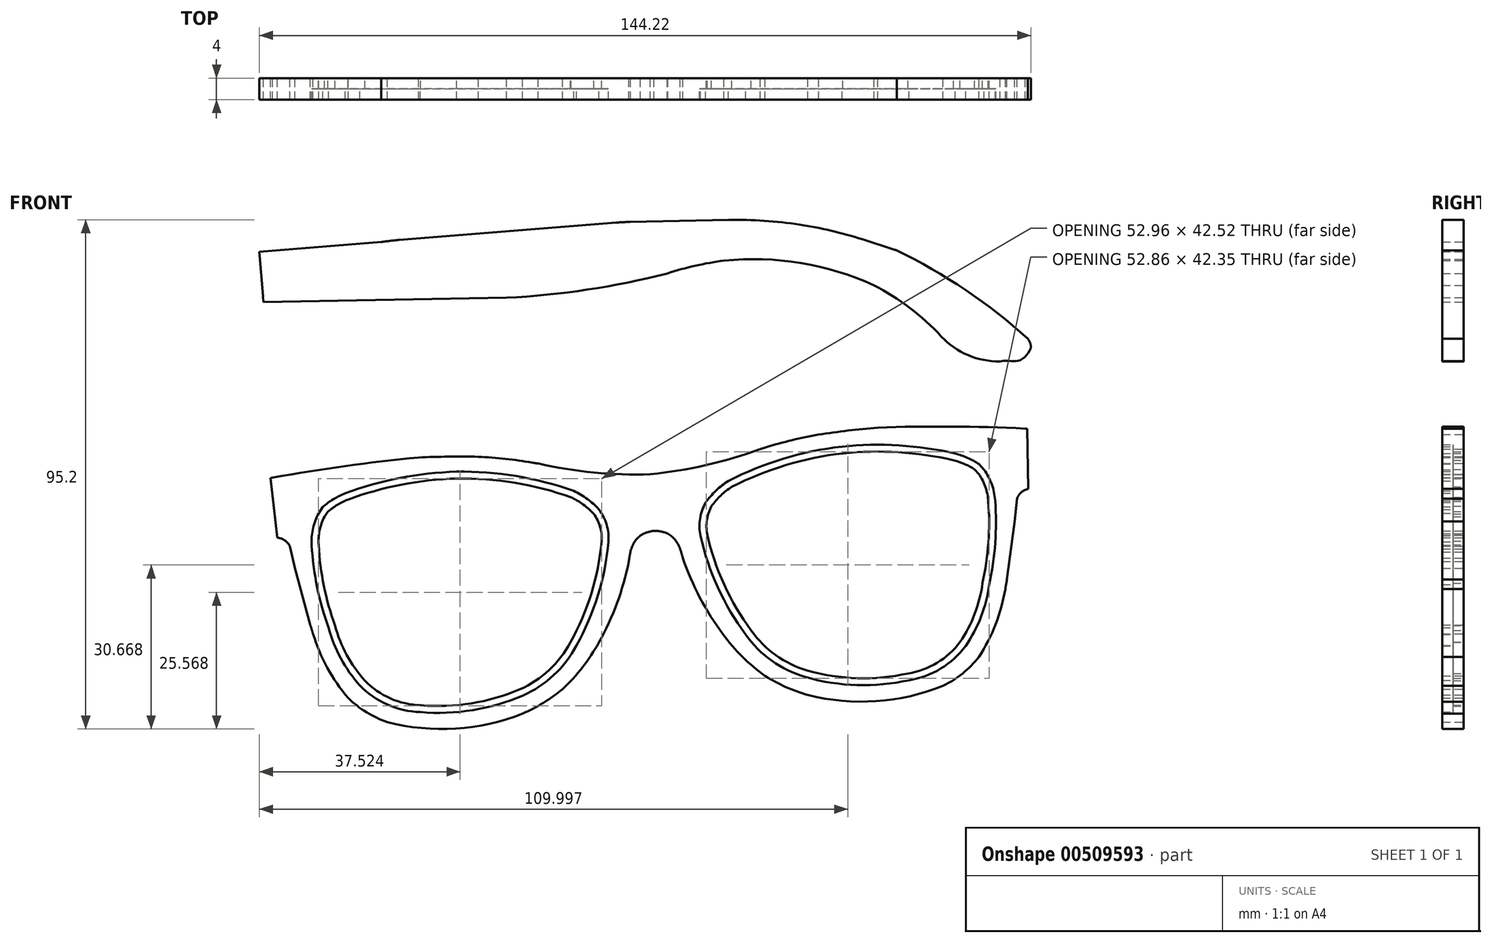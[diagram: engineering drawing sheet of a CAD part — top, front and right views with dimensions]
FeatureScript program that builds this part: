
annotation { "Feature Type Name" : "Feature", "Feature Type Description" : "" }
export const myFeature = defineFeature(function(context is Context, id is Id, definition is map)
    precondition{}
    {
        {
            var Q0;
            Q0=qCreatedBy(makeId("Front.planeOp"),FACE);
            var sketch = newSketch(context, id + "F0", { "sketchPlane" : qUnion([Q0])});
            skLineSegment(sketch, "E0", {"start": v(-3.2, 54.2) * mm, "end": v(-3.2, 54.2) * mm});
            skLineSegment(sketch, "E1", {"start": v(-1.57, 51.14) * mm, "end": v(-1.58, 51.11) * mm});
            skArc(sketch, "E2", {"start": v(-1.36, 53.99) * mm, "mid": v(-1.36, 53.99) * mm, "end": v(-1.36, 53.99) * mm});
            skArc(sketch, "E3", {"start": v(3.82, 54.3) * mm, "mid": v(3.82, 54.3) * mm, "end": v(3.82, 54.3) * mm});
            skArc(sketch, "E4", {"start": v(-1.34, 53.99) * mm, "mid": v(-1.34, 53.99) * mm, "end": v(-1.34, 53.99) * mm});
            skArc(sketch, "E5", {"start": v(-1.09, 54.17) * mm, "mid": v(-1.1, 54.16) * mm, "end": v(-1.12, 54.15) * mm});
            skArc(sketch, "E6", {"start": v(3.8, 54.29) * mm, "mid": v(3.8, 54.29) * mm, "end": v(3.8, 54.29) * mm});
            skArc(sketch, "E7", {"start": v(4.03, 54.34) * mm, "mid": v(4.03, 54.34) * mm, "end": v(4.03, 54.34) * mm});
            skArc(sketch, "E8", {"start": v(4.05, 54.34) * mm, "mid": v(4.05, 54.34) * mm, "end": v(4.05, 54.34) * mm});
            skArc(sketch, "E9", {"start": v(3.8, 54.47) * mm, "mid": v(3.78, 54.48) * mm, "end": v(3.76, 54.49) * mm});
            skLineSegment(sketch, "E10", {"start": v(-2.98, 54.16) * mm, "end": v(-2.97, 54.16) * mm});
            skLineSegment(sketch, "E11", {"start": v(-1.3, 51.11) * mm, "end": v(-1.3, 51.09) * mm});
            skArc(sketch, "E12", {"start": v(-1.1, 53.97) * mm, "mid": v(-1.1, 53.97) * mm, "end": v(-1.1, 53.97) * mm});
            skArc(sketch, "E13", {"start": v(-1.12, 53.97) * mm, "mid": v(-1.12, 53.97) * mm, "end": v(-1.12, 53.97) * mm});
            skArc(sketch, "E14", {"start": v(1.21, 56.17) * mm, "mid": v(1.21, 56.17) * mm, "end": v(1.21, 56.17) * mm});
            skLineSegment(sketch, "E15", {"start": v(-2.98, 54.16) * mm, "end": v(-2.98, 54.16) * mm});
            skLineSegment(sketch, "E16", {"start": v(-1.58, 51.14) * mm, "end": v(-1.59, 51.11) * mm});
            skLineSegment(sketch, "E17", {"start": v(-3.22, 54.2) * mm, "end": v(-3.21, 54.2) * mm});
            skArc(sketch, "E18", {"start": v(-14.4, 35.35) * mm, "mid": v(-10.5, 44.49) * mm, "end": v(-8.57, 54.23) * mm});
            skArc(sketch, "E19", {"start": v(-13.26, 34.74) * mm, "mid": v(-9.27, 44.12) * mm, "end": v(-7.3, 54.13) * mm});
            skArc(sketch, "E20", {"start": v(4.04, 54.34) * mm, "mid": v(4.04, 54.34) * mm, "end": v(4.04, 54.34) * mm});
            skArc(sketch, "E21", {"start": v(4.03, 54.34) * mm, "mid": v(4.02, 54.34) * mm, "end": v(4.02, 54.34) * mm});
            skArc(sketch, "E22", {"start": v(3.8, 54.3) * mm, "mid": v(3.8, 54.3) * mm, "end": v(3.8, 54.3) * mm});
            skArc(sketch, "E23", {"start": v(-1.35, 53.99) * mm, "mid": v(-1.35, 53.99) * mm, "end": v(-1.35, 53.99) * mm});
            skArc(sketch, "E24", {"start": v(-1.36, 54) * mm, "mid": v(-1.36, 54) * mm, "end": v(-1.37, 54) * mm});
            skArc(sketch, "E25", {"start": v(-1.3, 55.3) * mm, "mid": v(-2.53, 53.92) * mm, "end": v(-3.19, 52.2) * mm});
            skArc(sketch, "E26", {"start": v(-1.13, 53.97) * mm, "mid": v(-1.13, 53.97) * mm, "end": v(-1.13, 53.97) * mm});
            skArc(sketch, "E27", {"start": v(-1.11, 53.97) * mm, "mid": v(-1.11, 53.97) * mm, "end": v(-1.11, 53.97) * mm});
            skArc(sketch, "E28", {"start": v(-35.67, 65.95) * mm, "mid": v(-46.01, 64.8) * mm, "end": v(-56.04, 62) * mm});
            skArc(sketch, "E29", {"start": v(-35.7, 67.23) * mm, "mid": v(-46.26, 66.06) * mm, "end": v(-56.5, 63.2) * mm});
            skArc(sketch, "E30", {"start": v(-31.64, 70.02) * mm, "mid": v(-37.22, 70.04) * mm, "end": v(-42.79, 69.88) * mm});
            skArc(sketch, "E31", {"start": v(3.79, 54.47) * mm, "mid": v(3.77, 54.48) * mm, "end": v(3.75, 54.49) * mm});
            skLineSegment(sketch, "E32", {"start": v(-1.3, 51.12) * mm, "end": v(-1.3, 51.09) * mm});
            skArc(sketch, "E33", {"start": v(-1.1, 54.17) * mm, "mid": v(-1.11, 54.16) * mm, "end": v(-1.13, 54.15) * mm});
            skArc(sketch, "E34", {"start": v(-3.26, 51.64) * mm, "mid": v(-3.27, 51.63) * mm, "end": v(-3.27, 51.63) * mm});
            skArc(sketch, "E35", {"start": v(1.21, 56.17) * mm, "mid": v(1.2, 56.17) * mm, "end": v(1.2, 56.17) * mm});
            skArc(sketch, "E36", {"start": v(1.2, 56.17) * mm, "mid": v(-0.1, 55.87) * mm, "end": v(-1.3, 55.3) * mm});
            skArc(sketch, "E37", {"start": v(-19.62, 23.91) * mm, "mid": v(-18.69, 24.53) * mm, "end": v(-17.78, 25.18) * mm});
            skArc(sketch, "E38", {"start": v(-23.34, 22) * mm, "mid": v(-19.45, 24.01) * mm, "end": v(-15.89, 26.56) * mm});
            skArc(sketch, "E39", {"start": v(-23.83, 26.56) * mm, "mid": v(-18.36, 30.15) * mm, "end": v(-14.4, 35.35) * mm});
            skArc(sketch, "E40", {"start": v(-23.32, 25.38) * mm, "mid": v(-17.5, 29.2) * mm, "end": v(-13.26, 34.74) * mm});
            skArc(sketch, "E41", {"start": v(-56.5, 63.2) * mm, "mid": v(-58.7, 62.09) * mm, "end": v(-60.69, 60.64) * mm});
            skArc(sketch, "E42", {"start": v(-56.04, 62) * mm, "mid": v(-57.97, 61.03) * mm, "end": v(-59.73, 59.77) * mm});
            skLineSegment(sketch, "E43", {"start": v(-60.69, 60.64) * mm, "end": v(-61.5, 59.46) * mm});
            skArc(sketch, "E44", {"start": v(-60.4, 58.8) * mm, "mid": v(-61.3, 56.24) * mm, "end": v(-61.5, 53.54) * mm});
            skArc(sketch, "E45", {"start": v(-61.5, 53.54) * mm, "mid": v(-60.5, 45.88) * mm, "end": v(-58.42, 38.46) * mm});
            skArc(sketch, "E46", {"start": v(-62.77, 53.46) * mm, "mid": v(-61.77, 45.65) * mm, "end": v(-59.65, 38.07) * mm});
            skLineSegment(sketch, "E47", {"start": v(-65.9, 49.18) * mm, "end": v(-63.05, 38.58) * mm});
            skLineSegment(sketch, "E48", {"start": v(-65.9, 49.18) * mm, "end": v(-66.88, 53.32) * mm});
            skLineSegment(sketch, "E49", {"start": v(-59.73, 59.77) * mm, "end": v(-60.4, 58.8) * mm});
            skArc(sketch, "E50", {"start": v(-21.51, 68.92) * mm, "mid": v(-26.56, 69.64) * mm, "end": v(-31.64, 70.02) * mm});
            skArc(sketch, "E51", {"start": v(-7.3, 54.13) * mm, "mid": v(-7.64, 57.31) * mm, "end": v(-9.07, 60.17) * mm});
            skArc(sketch, "E52", {"start": v(-8.57, 54.23) * mm, "mid": v(-8.86, 56.92) * mm, "end": v(-10.06, 59.35) * mm});
            skArc(sketch, "E53", {"start": v(-10.06, 59.35) * mm, "mid": v(-12.03, 61.09) * mm, "end": v(-14.3, 62.44) * mm});
            skArc(sketch, "E54", {"start": v(-9.07, 60.17) * mm, "mid": v(-11.27, 62.12) * mm, "end": v(-13.8, 63.62) * mm});
            skArc(sketch, "E55", {"start": v(-14.3, 62.44) * mm, "mid": v(-24.82, 65.15) * mm, "end": v(-35.67, 65.95) * mm});
            skArc(sketch, "E56", {"start": v(-13.8, 63.62) * mm, "mid": v(-24.59, 66.4) * mm, "end": v(-35.7, 67.23) * mm});
            skArc(sketch, "E57", {"start": v(-42.79, 69.88) * mm, "mid": v(-56.47, 68.28) * mm, "end": v(-70.07, 66.12) * mm});
            skLineSegment(sketch, "E58", {"start": v(-70.17, 56.16) * mm, "end": v(-70.17, 56.15) * mm});
            skLineSegment(sketch, "E59", {"start": v(-67.76, 54.26) * mm, "end": v(-67.75, 54.25) * mm});
            skArc(sketch, "E60", {"start": v(-61.5, 59.46) * mm, "mid": v(-62.55, 56.55) * mm, "end": v(-62.77, 53.46) * mm});
            skLineSegment(sketch, "E61", {"start": v(-68.91, 57.09) * mm, "end": v(-68.91, 57.1) * mm});
            skArc(sketch, "E62", {"start": v(-66.88, 53.32) * mm, "mid": v(-67.84, 54.4) * mm, "end": v(-69.2, 54.87) * mm});
            skLineSegment(sketch, "E63", {"start": v(-70.48, 66.07) * mm, "end": v(-69.2, 54.87) * mm});
            skLineSegment(sketch, "E64", {"start": v(-70.07, 66.12) * mm, "end": v(-70.48, 66.07) * mm});
            skArc(sketch, "E65", {"start": v(-48.62, 20.4) * mm, "mid": v(-35.85, 19.2) * mm, "end": v(-23.34, 22) * mm});
            skArc(sketch, "E66", {"start": v(-63.05, 38.58) * mm, "mid": v(-62.8, 37.73) * mm, "end": v(-62.52, 36.89) * mm});
            skArc(sketch, "E67", {"start": v(-55.96, 24.9) * mm, "mid": v(-52.35, 22.13) * mm, "end": v(-48.2, 20.26) * mm});
            skArc(sketch, "E68", {"start": v(-62.52, 36.89) * mm, "mid": v(-59.87, 30.55) * mm, "end": v(-55.96, 24.9) * mm});
            skArc(sketch, "E69", {"start": v(-42.4, 23.56) * mm, "mid": v(-32.93, 23.9) * mm, "end": v(-23.83, 26.56) * mm});
            skArc(sketch, "E70", {"start": v(-42.48, 22.28) * mm, "mid": v(-32.7, 22.64) * mm, "end": v(-23.32, 25.38) * mm});
            skArc(sketch, "E71", {"start": v(-58.42, 38.46) * mm, "mid": v(-56.24, 32.97) * mm, "end": v(-52.85, 28.15) * mm});
            skArc(sketch, "E72", {"start": v(-52.85, 28.15) * mm, "mid": v(-48.07, 24.83) * mm, "end": v(-42.4, 23.56) * mm});
            skArc(sketch, "E73", {"start": v(-53.79, 27.27) * mm, "mid": v(-48.62, 23.67) * mm, "end": v(-42.48, 22.28) * mm});
            skArc(sketch, "E74", {"start": v(-59.65, 38.07) * mm, "mid": v(-57.35, 32.33) * mm, "end": v(-53.79, 27.27) * mm});
            skArc(sketch, "E75", {"start": v(-10.23, 33.32) * mm, "mid": v(-6.11, 41.58) * mm, "end": v(-3.5, 50.42) * mm});
            skArc(sketch, "E76", {"start": v(-6.4, 39.18) * mm, "mid": v(-6.39, 39.19) * mm, "end": v(-6.38, 39.2) * mm});
            skArc(sketch, "E77", {"start": v(-15.89, 26.56) * mm, "mid": v(-12.14, 30.67) * mm, "end": v(-9.07, 35.31) * mm});
            skArc(sketch, "E78", {"start": v(-3.19, 52.2) * mm, "mid": v(-3.36, 51.3) * mm, "end": v(-3.5, 50.42) * mm});
            skArc(sketch, "E79", {"start": v(-20.47, 68.76) * mm, "mid": v(-10.04, 67.08) * mm, "end": v(0.52, 66.75) * mm});
            skArc(sketch, "E80", {"start": v(4.02, 54.34) * mm, "mid": v(4.02, 54.34) * mm, "end": v(4.02, 54.34) * mm});
            skLineSegment(sketch, "E81", {"start": v(4.62, 51.54) * mm, "end": v(4.63, 51.52) * mm});
            skLineSegment(sketch, "E82", {"start": v(4.63, 51.54) * mm, "end": v(4.64, 51.52) * mm});
            skArc(sketch, "E83", {"start": v(-1.37, 54) * mm, "mid": v(-1.37, 54) * mm, "end": v(-1.37, 54) * mm});
            skLineSegment(sketch, "E84", {"start": v(5.62, 54.72) * mm, "end": v(5.62, 54.72) * mm});
            skLineSegment(sketch, "E85", {"start": v(4.35, 51.48) * mm, "end": v(4.35, 51.46) * mm});
            skLineSegment(sketch, "E86", {"start": v(4.36, 51.48) * mm, "end": v(4.36, 51.46) * mm});
            skArc(sketch, "E87", {"start": v(6.08, 52.8) * mm, "mid": v(5.2, 54.42) * mm, "end": v(3.81, 55.64) * mm});
            skLineSegment(sketch, "E88", {"start": v(5.62, 54.72) * mm, "end": v(5.61, 54.72) * mm});
            skArc(sketch, "E89", {"start": v(63.72, 61.7) * mm, "mid": v(63.18, 64.35) * mm, "end": v(61.95, 66.77) * mm});
            skLineSegment(sketch, "E90", {"start": v(61.16, 67.65) * mm, "end": v(61.95, 66.77) * mm});
            skArc(sketch, "E91", {"start": v(-1.14, 53.97) * mm, "mid": v(-1.14, 53.97) * mm, "end": v(-1.14, 53.97) * mm});
            skArc(sketch, "E92", {"start": v(1.2, 56.17) * mm, "mid": v(1.2, 56.17) * mm, "end": v(1.2, 56.17) * mm});
            skArc(sketch, "E93", {"start": v(3.78, 54.29) * mm, "mid": v(3.78, 54.29) * mm, "end": v(3.78, 54.29) * mm});
            skArc(sketch, "E94", {"start": v(3.78, 54.47) * mm, "mid": v(3.76, 54.48) * mm, "end": v(3.74, 54.48) * mm});
            skArc(sketch, "E95", {"start": v(3.81, 55.64) * mm, "mid": v(2.54, 56.04) * mm, "end": v(1.2, 56.17) * mm});
            skArc(sketch, "E96", {"start": v(-1.1, 54.17) * mm, "mid": v(-1.12, 54.16) * mm, "end": v(-1.14, 54.15) * mm});
            skLineSegment(sketch, "E97", {"start": v(5.85, 54.8) * mm, "end": v(5.85, 54.8) * mm});
            skLineSegment(sketch, "E98", {"start": v(5.84, 54.8) * mm, "end": v(5.84, 54.8) * mm});
            skArc(sketch, "E99", {"start": v(10.88, 61.47) * mm, "mid": v(9.83, 58.45) * mm, "end": v(9.9, 55.25) * mm});
            skArc(sketch, "E100", {"start": v(11.96, 60.78) * mm, "mid": v(11.1, 58.22) * mm, "end": v(11.16, 55.52) * mm});
            skArc(sketch, "E101", {"start": v(6.23, 52.25) * mm, "mid": v(6.23, 52.25) * mm, "end": v(6.23, 52.26) * mm});
            skArc(sketch, "E102", {"start": v(6.62, 51.08) * mm, "mid": v(6.37, 51.94) * mm, "end": v(6.08, 52.8) * mm});
            skArc(sketch, "E103", {"start": v(11.16, 55.52) * mm, "mid": v(14.33, 46.1) * mm, "end": v(19.38, 37.55) * mm});
            skArc(sketch, "E104", {"start": v(9.9, 55.25) * mm, "mid": v(13.16, 45.58) * mm, "end": v(18.34, 36.8) * mm});
            skArc(sketch, "E105", {"start": v(6.62, 51.08) * mm, "mid": v(10.36, 42.65) * mm, "end": v(15.52, 35) * mm});
            skArc(sketch, "E106", {"start": v(10.94, 40.33) * mm, "mid": v(10.94, 40.32) * mm, "end": v(10.95, 40.3) * mm});
            skArc(sketch, "E107", {"start": v(14.1, 36.82) * mm, "mid": v(17.75, 32.62) * mm, "end": v(22, 29.03) * mm});
            skArc(sketch, "E108", {"start": v(62.63, 46.35) * mm, "mid": v(63.74, 53.98) * mm, "end": v(63.72, 61.7) * mm});
            skArc(sketch, "E109", {"start": v(63.9, 46.13) * mm, "mid": v(65.02, 53.91) * mm, "end": v(65, 61.78) * mm});
            skLineSegment(sketch, "E110", {"start": v(68.66, 57.95) * mm, "end": v(69.08, 62.18) * mm});
            skLineSegment(sketch, "E111", {"start": v(68.66, 57.95) * mm, "end": v(67.2, 47.07) * mm});
            skArc(sketch, "E112", {"start": v(66.9, 45.32) * mm, "mid": v(67.06, 46.2) * mm, "end": v(67.2, 47.07) * mm});
            skArc(sketch, "E113", {"start": v(58.44, 35.4) * mm, "mid": v(61.18, 40.63) * mm, "end": v(62.63, 46.35) * mm});
            skArc(sketch, "E114", {"start": v(59.49, 34.65) * mm, "mid": v(62.36, 40.13) * mm, "end": v(63.9, 46.13) * mm});
            skArc(sketch, "E115", {"start": v(61.95, 32.6) * mm, "mid": v(65.1, 38.7) * mm, "end": v(66.9, 45.32) * mm});
            skArc(sketch, "E116", {"start": v(24.05, 27.9) * mm, "mid": v(25.04, 27.38) * mm, "end": v(26.05, 26.89) * mm});
            skArc(sketch, "E117", {"start": v(22, 29.03) * mm, "mid": v(25.87, 26.97) * mm, "end": v(29.98, 25.48) * mm});
            skArc(sketch, "E118", {"start": v(19.38, 37.55) * mm, "mid": v(24, 32.91) * mm, "end": v(29.87, 30.06) * mm});
            skArc(sketch, "E119", {"start": v(18.34, 36.8) * mm, "mid": v(23.25, 31.86) * mm, "end": v(29.52, 28.82) * mm});
            skArc(sketch, "E120", {"start": v(54.85, 26.97) * mm, "mid": v(58.73, 29.37) * mm, "end": v(61.95, 32.6) * mm});
            skArc(sketch, "E121", {"start": v(48.68, 29.5) * mm, "mid": v(54.14, 31.5) * mm, "end": v(58.44, 35.4) * mm});
            skArc(sketch, "E122", {"start": v(48.92, 28.23) * mm, "mid": v(54.83, 30.41) * mm, "end": v(59.49, 34.65) * mm});
            skArc(sketch, "E123", {"start": v(29.87, 30.06) * mm, "mid": v(39.24, 28.61) * mm, "end": v(48.68, 29.5) * mm});
            skArc(sketch, "E124", {"start": v(29.98, 25.48) * mm, "mid": v(42.75, 24.32) * mm, "end": v(55.25, 27.17) * mm});
            skArc(sketch, "E125", {"start": v(29.52, 28.82) * mm, "mid": v(39.18, 27.33) * mm, "end": v(48.92, 28.23) * mm});
            skArc(sketch, "E126", {"start": v(65, 61.78) * mm, "mid": v(64.38, 64.82) * mm, "end": v(62.96, 67.57) * mm});
            skLineSegment(sketch, "E127", {"start": v(69.84, 63.22) * mm, "end": v(69.83, 63.22) * mm});
            skArc(sketch, "E128", {"start": v(71.19, 64.02) * mm, "mid": v(69.9, 63.38) * mm, "end": v(69.08, 62.18) * mm});
            skLineSegment(sketch, "E129", {"start": v(70.61, 66.18) * mm, "end": v(70.61, 66.19) * mm});
            skLineSegment(sketch, "E130", {"start": v(71.99, 65.42) * mm, "end": v(71.99, 65.42) * mm});
            skLineSegment(sketch, "E131", {"start": v(62, 68.63) * mm, "end": v(62.96, 67.57) * mm});
            skArc(sketch, "E132", {"start": v(62, 68.63) * mm, "mid": v(59.84, 69.81) * mm, "end": v(57.52, 70.64) * mm});
            skArc(sketch, "E133", {"start": v(61.16, 67.65) * mm, "mid": v(59.25, 68.67) * mm, "end": v(57.2, 69.39) * mm});
            skArc(sketch, "E134", {"start": v(70.6, 75.29) * mm, "mid": v(56.82, 75.67) * mm, "end": v(43.05, 75.47) * mm});
            skArc(sketch, "E135", {"start": v(57.52, 70.64) * mm, "mid": v(47, 72.14) * mm, "end": v(36.37, 71.93) * mm});
            skArc(sketch, "E136", {"start": v(57.2, 69.39) * mm, "mid": v(46.9, 70.86) * mm, "end": v(36.5, 70.65) * mm});
            skArc(sketch, "E137", {"start": v(0.52, 66.75) * mm, "mid": v(10.95, 68.45) * mm, "end": v(21.07, 71.47) * mm});
            skArc(sketch, "E138", {"start": v(43.05, 75.47) * mm, "mid": v(37.5, 74.91) * mm, "end": v(31.98, 74.16) * mm});
            skArc(sketch, "E139", {"start": v(15.76, 64.4) * mm, "mid": v(13.7, 62.76) * mm, "end": v(11.96, 60.78) * mm});
            skArc(sketch, "E140", {"start": v(15.12, 65.5) * mm, "mid": v(12.8, 63.7) * mm, "end": v(10.88, 61.47) * mm});
            skArc(sketch, "E141", {"start": v(31.98, 74.16) * mm, "mid": v(27, 73.13) * mm, "end": v(22.08, 71.76) * mm});
            skArc(sketch, "E142", {"start": v(36.5, 70.65) * mm, "mid": v(25.85, 68.45) * mm, "end": v(15.76, 64.4) * mm});
            skArc(sketch, "E143", {"start": v(36.37, 71.93) * mm, "mid": v(25.46, 69.67) * mm, "end": v(15.12, 65.5) * mm});
            skLineSegment(sketch, "E144", {"start": v(71, 75.29) * mm, "end": v(71.19, 64.02) * mm});
            skLineSegment(sketch, "E145", {"start": v(70.6, 75.29) * mm, "end": v(71, 75.29) * mm});
            skArc(sketch, "E146", {"start": v(-21.51, 68.92) * mm, "mid": v(-21, 68.84) * mm, "end": v(-20.47, 68.76) * mm});
            skArc(sketch, "E147", {"start": v(21.07, 71.47) * mm, "mid": v(21.58, 71.6) * mm, "end": v(22.08, 71.76) * mm});
            skLineSegment(sketch, "E148", {"start": v(28.57, 113.41) * mm, "end": v(28.3, 113.46) * mm});
            skLineSegment(sketch, "E149", {"start": v(-46.43, 110.56) * mm, "end": v(-5.9, 113.8) * mm});
            skLineSegment(sketch, "E150", {"start": v(-3.22, 113.93) * mm, "end": v(15.19, 114.3) * mm});
            skArc(sketch, "E151", {"start": v(23.62, 114.17) * mm, "mid": v(23.45, 114.2) * mm, "end": v(23.28, 114.22) * mm});
            skArc(sketch, "E152", {"start": v(-3.22, 113.93) * mm, "mid": v(-4.56, 113.88) * mm, "end": v(-5.9, 113.8) * mm});
            skArc(sketch, "E153", {"start": v(-46.43, 110.56) * mm, "mid": v(-48.1, 110.4) * mm, "end": v(-49.76, 110.17) * mm});
            skArc(sketch, "E154", {"start": v(28.57, 113.41) * mm, "mid": v(21.9, 114.15) * mm, "end": v(15.19, 114.3) * mm});
            skLineSegment(sketch, "E155", {"start": v(40.18, 110.67) * mm, "end": v(46.2, 108.75) * mm});
            skArc(sketch, "E156", {"start": v(40.18, 110.67) * mm, "mid": v(34.29, 112.3) * mm, "end": v(28.3, 113.46) * mm});
            skLineSegment(sketch, "E157", {"start": v(-49.76, 110.17) * mm, "end": v(-72.56, 108.34) * mm});
            skLineSegment(sketch, "E158", {"start": v(-71.9, 100.07) * mm, "end": v(-71.88, 99.94) * mm});
            skArc(sketch, "E159", {"start": v(14.3, 106.7) * mm, "mid": v(8.64, 105.67) * mm, "end": v(3.1, 104.1) * mm});
            skArc(sketch, "E160", {"start": v(42.36, 102.1) * mm, "mid": v(28.63, 106.25) * mm, "end": v(14.3, 106.7) * mm});
            skArc(sketch, "E161", {"start": v(54.96, 92.5) * mm, "mid": v(49.07, 97.83) * mm, "end": v(42.36, 102.1) * mm});
            skArc(sketch, "E162", {"start": v(46.6, 108.61) * mm, "mid": v(46.4, 108.68) * mm, "end": v(46.2, 108.75) * mm});
            skArc(sketch, "E163", {"start": v(54.96, 92.5) * mm, "mid": v(59.93, 89.01) * mm, "end": v(65.88, 87.85) * mm});
            skFitSpline(sketch, "E164", {"points": [v(71.14, 92.07) * mm, v(71.39, 91.63) * mm, v(71.63, 90.38) * mm, v(69.72, 88.12) * mm, v(67.47, 87.96) * mm, v(65.88, 87.85) * mm]});
            skLineSegment(sketch, "E165", {"start": v(-72.56, 108.34) * mm, "end": v(-71.8, 98.92) * mm});
            skArc(sketch, "E166", {"start": v(71.14, 92.07) * mm, "mid": v(59.45, 101.2) * mm, "end": v(46.6, 108.61) * mm});
            skLineSegment(sketch, "E167", {"start": v(-71.8, 98.92) * mm, "end": v(-26.37, 99.75) * mm});
            skArc(sketch, "E168", {"start": v(-35.98, 99.57) * mm, "mid": v(-15.97, 100.62) * mm, "end": v(3.71, 104.3) * mm});
            skSolve(sketch);
        }
        {
            var Q0;
            Q0=makeQuery(id+"F0.imprint","IMPRINT",FACE,{"disambiguationData":[TD([[makeQuery(id+"F0.imprint","IMPRINT",EDGE,{"derivedFrom":sQuery(id+"F0.wireOp",EDGE,"E19")}),-1.0]])]});
            extrude(context, id + "F1", {"entities" : qUnion([Q0]), "depth" : 4 * mm});
        }
        {
            var Q0;
            Q0=makeQuery(id+"F0.imprint","IMPRINT",FACE,{"disambiguationData":[TD([[makeQuery(id+"F0.imprint","IMPRINT",EDGE,{"derivedFrom":sQuery(id+"F0.wireOp",EDGE,"E18")}),-1.0]])]});
            var Q1;
            Q1=makeQuery(id+"F0.imprint","IMPRINT",FACE,{"disambiguationData":[TD([[makeQuery(id+"F0.imprint","IMPRINT",EDGE,{"derivedFrom":sQuery(id+"F0.wireOp",EDGE,"E89")}),-1.0]])]});
            extrude(context, id + "F2", {"entities" : qUnion([Q0, Q1]), "operationType" : NewBodyOperationType.ADD, "depth" : 2 * mm});
        }
        {
            var Q0;
            Q0=makeQuery(id+"F0.imprint","IMPRINT",FACE,{"disambiguationData":[TD([[makeQuery(id+"F0.imprint","IMPRINT",EDGE,{"derivedFrom":sQuery(id+"F0.wireOp",EDGE,"E149")}),-1.0]])]});
            extrude(context, id + "F3", {"entities" : qUnion([Q0]), "depth" : 4 * mm});
        }
    });
